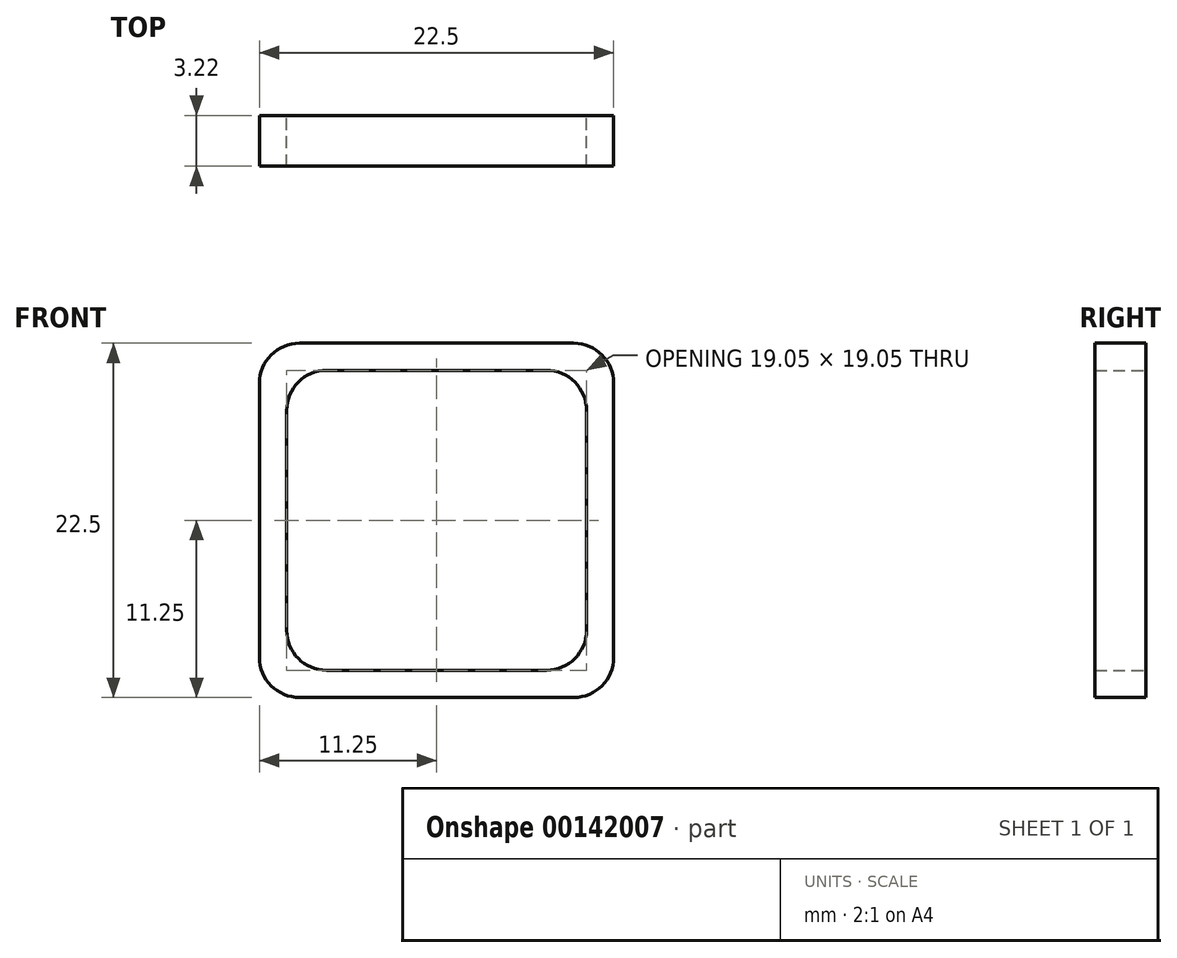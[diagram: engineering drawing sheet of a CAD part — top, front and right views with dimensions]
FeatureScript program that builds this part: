
annotation { "Feature Type Name" : "Feature", "Feature Type Description" : "" }
export const myFeature = defineFeature(function(context is Context, id is Id, definition is map)
    precondition{}
    {
        {
            var Q0;
            Q0=qCreatedBy(makeId("Front.planeOp"),FACE);
            var sketch = newSketch(context, id + "F0", { "sketchPlane" : qUnion([Q0])});
            skLineSegment(sketch, "E0.bottom", {"start": v(11.25, 11.25) * mm, "end": v(-11.25, 11.25) * mm});
            skLineSegment(sketch, "E0.top", {"start": v(11.25, -11.25) * mm, "end": v(-11.25, -11.25) * mm});
            skLineSegment(sketch, "E0.left", {"start": v(11.25, 11.25) * mm, "end": v(11.25, -11.25) * mm});
            skLineSegment(sketch, "E0.right", {"start": v(-11.25, 11.25) * mm, "end": v(-11.25, -11.25) * mm});
            skPoint(sketch, "E0.middle", {"position": v(0, 0) * mm});
            skLineSegment(sketch, "E1.0", {"start": v(9.52, -9.52) * mm, "end": v(-9.53, -9.52) * mm});
            skLineSegment(sketch, "E1.1", {"start": v(9.52, 9.52) * mm, "end": v(9.52, -9.52) * mm});
            skLineSegment(sketch, "E1.2", {"start": v(9.52, 9.52) * mm, "end": v(-9.53, 9.52) * mm});
            skLineSegment(sketch, "E1.3", {"start": v(-9.53, 9.52) * mm, "end": v(-9.53, -9.52) * mm});
            skSolve(sketch);
        }
        {
            var Q0;
            Q0=makeQuery(id+"F0.imprint","IMPRINT",FACE,{"disambiguationData":[TD([[makeQuery(id+"F0.imprint","IMPRINT",EDGE,{"derivedFrom":sQuery(id+"F0.wireOp",EDGE,"E0.bottom")}),1.0]])]});
            var Q1;
            Q1=sQuery(id+"F0.wireOp",EDGE,"E0.right");
            var Q2;
            Q2=sQuery(id+"F0.wireOp",EDGE,"E1.3");
            extrude(context, id + "F1", {"entities" : qUnion([Q0]), "surfaceEntities" : qUnion([Q1, Q2]), "depth" : 32.25 / 20 * mm, "hasSecondDirection" : true, "secondDirectionOppositeDirection" : true, "secondDirectionDepth" : 32.25 / 20 * mm});
        }
        {
            var Q0;
            Q0=makeQuery(id+"F1.opExtrude","SWEPT_EDGE",EDGE,{"disambiguationData":[OSD([sQuery(id+"F0.wireOp",EDGE,"E0.bottom"),sQuery(id+"F0.wireOp",EDGE,"E0.right")])]});
            var Q1;
            Q1=makeQuery(id+"F1.opExtrude","SWEPT_EDGE",EDGE,{"disambiguationData":[OSD([sQuery(id+"F0.wireOp",EDGE,"E0.bottom"),sQuery(id+"F0.wireOp",EDGE,"E0.left")])]});
            var Q2;
            Q2=makeQuery(id+"F1.opExtrude","SWEPT_EDGE",EDGE,{"disambiguationData":[OSD([sQuery(id+"F0.wireOp",EDGE,"E0.top"),sQuery(id+"F0.wireOp",EDGE,"E0.right")])]});
            var Q3;
            Q3=makeQuery(id+"F1.opExtrude","SWEPT_EDGE",EDGE,{"disambiguationData":[OSD([sQuery(id+"F0.wireOp",EDGE,"E0.top"),sQuery(id+"F0.wireOp",EDGE,"E0.left")])]});
            var Q4;
            Q4=makeQuery(id+"F1.opExtrude","SWEPT_EDGE",EDGE,{"disambiguationData":[OSD([sQuery(id+"F0.wireOp",EDGE,"E1.2"),sQuery(id+"F0.wireOp",EDGE,"E1.3")])]});
            var Q5;
            Q5=makeQuery(id+"F1.opExtrude","SWEPT_EDGE",EDGE,{"disambiguationData":[OSD([sQuery(id+"F0.wireOp",EDGE,"E1.1"),sQuery(id+"F0.wireOp",EDGE,"E1.2")])]});
            var Q6;
            Q6=makeQuery(id+"F1.opExtrude","SWEPT_EDGE",EDGE,{"disambiguationData":[OSD([sQuery(id+"F0.wireOp",EDGE,"E1.0"),sQuery(id+"F0.wireOp",EDGE,"E1.1")])]});
            var Q7;
            Q7=makeQuery(id+"F1.opExtrude","SWEPT_EDGE",EDGE,{"disambiguationData":[OSD([sQuery(id+"F0.wireOp",EDGE,"E1.0"),sQuery(id+"F0.wireOp",EDGE,"E1.3")])]});
            fillet(context, id + "F2", {"entities" : qUnion([Q0, Q1, Q2, Q3, Q4, Q5, Q6, Q7]), "radius" : 2.54 * mm, "tangentPropagation" : true, "allowEdgeOverflow" : false});
        }
        {
            var Q0;
            Q0=makeQuery(id+"F1.opExtrude","SWEPT_FACE",FACE,{"disambiguationData":[OSD([sQuery(id+"F0.wireOp",EDGE,"E0.bottom")])]});
            var sketch = newSketch(context, id + "F3", { "sketchPlane" : qUnion([Q0])});
            skLineSegment(sketch, "E2.bottom", {"start": v(-11.25, 161.25) * mm, "end": v(11.25, 161.25) * mm});
            skLineSegment(sketch, "E2.top", {"start": v(-11.25, 123.15) * mm, "end": v(11.25, 123.15) * mm});
            skLineSegment(sketch, "E2.left", {"start": v(-11.25, 161.25) * mm, "end": v(-11.25, 123.15) * mm});
            skLineSegment(sketch, "E2.right", {"start": v(11.25, 161.25) * mm, "end": v(11.25, 123.15) * mm});
            skLineSegment(sketch, "E3", {"start": v(0, 161.25) * mm, "end": v(0, 123.15) * mm, "construction": true});
            skLineSegment(sketch, "E4", {"start": v(-11.25, 142.2) * mm, "end": v(11.25, 142.2) * mm, "construction": true});
            skLineSegment(sketch, "E5.bottom", {"start": v(6.35, 150.14) * mm, "end": v(-6.35, 150.14) * mm, "construction": true});
            skLineSegment(sketch, "E5.top", {"start": v(6.35, 134.26) * mm, "end": v(-6.35, 134.26) * mm, "construction": true});
            skLineSegment(sketch, "E5.left", {"start": v(6.35, 150.14) * mm, "end": v(6.35, 134.26) * mm, "construction": true});
            skLineSegment(sketch, "E5.right", {"start": v(-6.35, 150.14) * mm, "end": v(-6.35, 134.26) * mm, "construction": true});
            skPoint(sketch, "E5.middle", {"position": v(0, 142.2) * mm});
            skSolve(sketch);
        }
        {
            var Q0;
            Q0=sQuery(id+"F3.wireOp",VERTEX,"E5.left.start");
            var Q1;
            Q1=sQuery(id+"F3.wireOp",VERTEX,"E5.top.start");
            var Q2;
            Q2=sQuery(id+"F3.wireOp",VERTEX,"E5.bottom.end");
            var Q3;
            Q3=sQuery(id+"F3.wireOp",VERTEX,"E5.top.end");
            var Q4;
            Q4=makeQuery(id+"F1.opExtrude","SWEPT_BODY",BODY,{"disambiguationData":[OSD([sQuery(id+"F0.wireOp",EDGE,"E0.bottom"),sQuery(id+"F0.wireOp",EDGE,"E0.top"),sQuery(id+"F0.wireOp",EDGE,"E0.left"),sQuery(id+"F0.wireOp",EDGE,"E0.right"),sQuery(id+"F0.wireOp",EDGE,"E1.0"),sQuery(id+"F0.wireOp",EDGE,"E1.1"),sQuery(id+"F0.wireOp",EDGE,"E1.2"),sQuery(id+"F0.wireOp",EDGE,"E1.3")])]});
            hole(context, id + "F4", {"style" : HoleStyle.SIMPLE, "endStyle" : HoleEndStyle.THROUGH, "standardTappedOrClearance" : lookupTablePath({ "standard" : "ISO", "fit" : "Normal", "size" : "M3", "type" : "Clearance" }), "standardBlindInLast" : lookupTablePath({ "fit" : "Standard", "standard" : "ISO", "size" : "M3", "type" : "Clearance" }), "holeDiameter" : 3.3 * mm, "locations" : qUnion([Q0, Q1, Q2, Q3]), "scope" : qUnion([Q4]), "isTappedThrough" : true});
        }
    });
